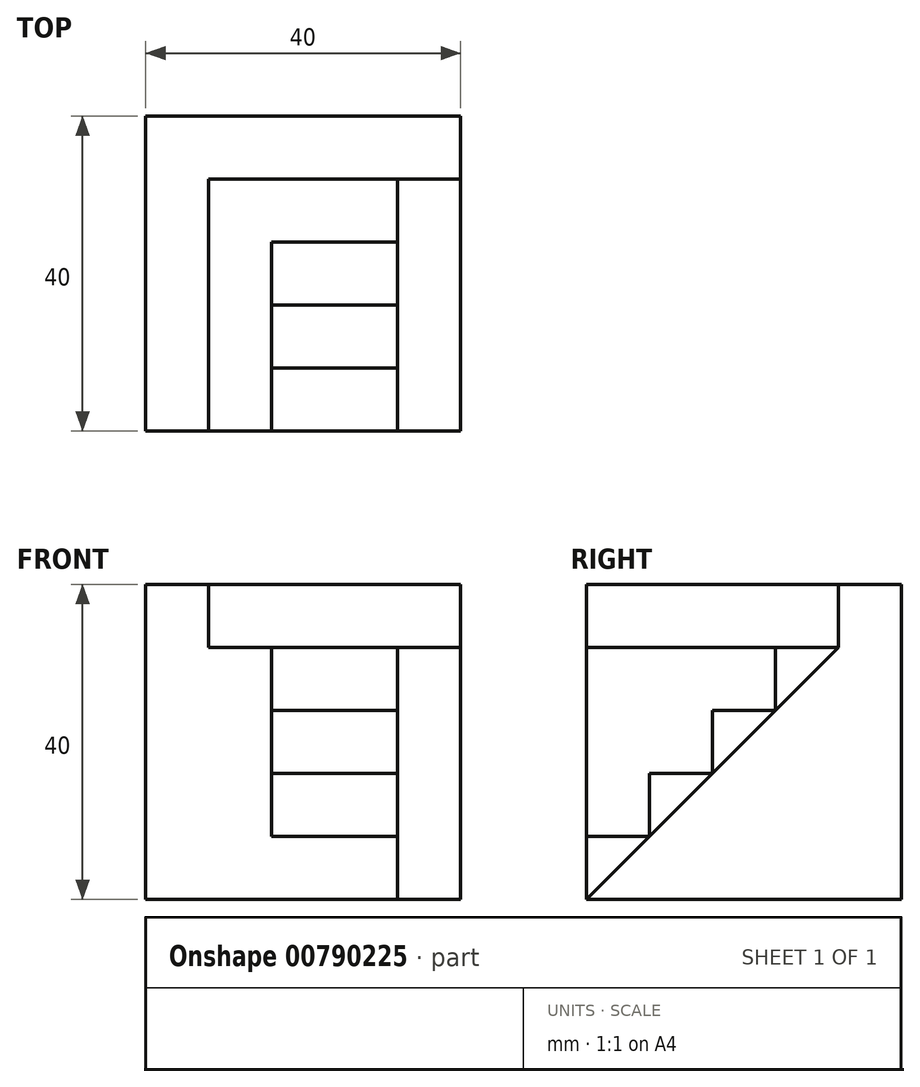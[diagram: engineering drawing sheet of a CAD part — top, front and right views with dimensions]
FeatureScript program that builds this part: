
annotation { "Feature Type Name" : "Feature", "Feature Type Description" : "" }
export const myFeature = defineFeature(function(context is Context, id is Id, definition is map)
    precondition{}
    {
        {
            var Q0;
            Q0=qCreatedBy(makeId("Top.planeOp"),FACE);
            var sketch = newSketch(context, id + "F0", { "sketchPlane" : qUnion([Q0])});
            skLineSegment(sketch, "E0.bottom", {"start": v(-20, -20) * mm, "end": v(20, -20) * mm});
            skLineSegment(sketch, "E0.top", {"start": v(-20, 20) * mm, "end": v(20, 20) * mm});
            skLineSegment(sketch, "E0.left", {"start": v(-20, -20) * mm, "end": v(-20, 20) * mm});
            skLineSegment(sketch, "E0.right", {"start": v(20, -20) * mm, "end": v(20, 20) * mm});
            skPoint(sketch, "E0.middle", {"position": v(0, 0) * mm});
            skLineSegment(sketch, "E1", {"start": v(-12, -20) * mm, "end": v(-12, 12) * mm});
            skLineSegment(sketch, "E2", {"start": v(-12, 12) * mm, "end": v(20, 12) * mm});
            skLineSegment(sketch, "E3", {"start": v(12, 12) * mm, "end": v(12, -20) * mm});
            skLineSegment(sketch, "E4", {"start": v(-4, -12) * mm, "end": v(12, -12) * mm});
            skLineSegment(sketch, "E5", {"start": v(-4, -20) * mm, "end": v(-4, 4) * mm});
            skLineSegment(sketch, "E6", {"start": v(-4, -4) * mm, "end": v(12, -4) * mm});
            skLineSegment(sketch, "E7", {"start": v(-4, 4) * mm, "end": v(12, 4) * mm});
            skPoint(sketch, "E8.orphan", {"position": v(12, 20) * mm});
            skPoint(sketch, "E9.orphan", {"position": v(-4, 12) * mm});
            skPoint(sketch, "E10.orphan", {"position": v(20, 4) * mm});
            skPoint(sketch, "E11.orphan", {"position": v(20, -12) * mm});
            skSolve(sketch);
        }
        {
            var Q0;
            {var subQ1=sQuery(id+"F0.wireOp",EDGE,"E0.right");var subQ6=sQuery(id+"F0.wireOp",EDGE,"E0.bottom");var subQ7=makeQuery(id+"F0.imprint","INTERSECT",VERTEX,{"derivedFrom":[subQ6,subQ1]});Q0=makeQuery(id+"F0.imprint","IMPRINT",FACE,{"disambiguationData":[TD([[makeQuery(id+"F0.imprint","IMPRINT",EDGE,{"disambiguationData":[TD([[subQ7,1.0]])],"derivedFrom":subQ6}),1.0]])]});}
            extrude(context, id + "F1", {"entities" : qUnion([Q0]), "depth" : 32 * mm, "offsetDistance" : 25 * mm});
        }
        {
            var Q0;
            Q0=makeQuery(id+"F1.opExtrude","SWEPT_FACE",FACE,{"disambiguationData":[OSD([sQuery(id+"F0.wireOp",EDGE,"E0.right")])]});
            var sketch = newSketch(context, id + "F2", { "sketchPlane" : qUnion([Q0])});
            skLineSegment(sketch, "E12", {"start": v(12, 32) * mm, "end": v(-20, 0) * mm});
            skSolve(sketch);
        }
        {
            var Q0;
            Q0=makeQuery(id+"F2.imprint","IMPRINT",FACE,{"disambiguationData":[TD([[makeQuery(id+"F2.imprint","IMPRINT",EDGE,{"derivedFrom":sQuery(id+"F2.wireOp",EDGE,"E12")}),-1.0]])]});
            extrude(context, id + "F3", {"entities" : qUnion([Q0]), "operationType" : NewBodyOperationType.REMOVE, "oppositeDirection" : true, "depth" : 25 * mm, "offsetDistance" : 25 * mm});
        }
        {
            var Q0;
            {var subQ1=sQuery(id+"F0.wireOp",EDGE,"E0.top");Q0=makeQuery(id+"F0.imprint","IMPRINT",FACE,{"disambiguationData":[TD([[makeQuery(id+"F0.imprint","IMPRINT",EDGE,{"derivedFrom":subQ1}),-1.0]])]});}
            extrude(context, id + "F4", {"entities" : qUnion([Q0]), "operationType" : NewBodyOperationType.ADD, "depth" : 40 * mm, "offsetDistance" : 25 * mm});
        }
        {
            var Q0;
            {var subQ1=sQuery(id+"F0.wireOp",EDGE,"E1");Q0=makeQuery(id+"F0.imprint","IMPRINT",FACE,{"disambiguationData":[TD([[makeQuery(id+"F0.imprint","IMPRINT",EDGE,{"derivedFrom":subQ1}),-1.0]])]});}
            extrude(context, id + "F5", {"entities" : qUnion([Q0]), "operationType" : NewBodyOperationType.ADD, "depth" : 32 * mm, "offsetDistance" : 25 * mm});
        }
        {
            var Q0;
            {var subQ0=sQuery(id+"F0.wireOp",EDGE,"E6");Q0=makeQuery(id+"F0.imprint","IMPRINT",FACE,{"disambiguationData":[TD([[makeQuery(id+"F0.imprint","IMPRINT",EDGE,{"derivedFrom":subQ0}),1.0]])]});}
            extrude(context, id + "F6", {"entities" : qUnion([Q0]), "operationType" : NewBodyOperationType.ADD, "depth" : 24 * mm, "offsetDistance" : 25 * mm});
        }
        {
            var Q0;
            {var subQ0=sQuery(id+"F0.wireOp",EDGE,"E4");Q0=makeQuery(id+"F0.imprint","IMPRINT",FACE,{"disambiguationData":[TD([[makeQuery(id+"F0.imprint","IMPRINT",EDGE,{"derivedFrom":subQ0}),1.0]])]});}
            extrude(context, id + "F7", {"entities" : qUnion([Q0]), "operationType" : NewBodyOperationType.ADD, "depth" : 16 * mm, "offsetDistance" : 25 * mm});
        }
        {
            var Q0;
            {var subQ5=sQuery(id+"F0.wireOp",EDGE,"E4");Q0=makeQuery(id+"F0.imprint","IMPRINT",FACE,{"disambiguationData":[TD([[makeQuery(id+"F0.imprint","IMPRINT",EDGE,{"derivedFrom":subQ5}),-1.0]])]});}
            extrude(context, id + "F8", {"entities" : qUnion([Q0]), "operationType" : NewBodyOperationType.ADD, "depth" : 8 * mm, "offsetDistance" : 25 * mm});
        }
    });
